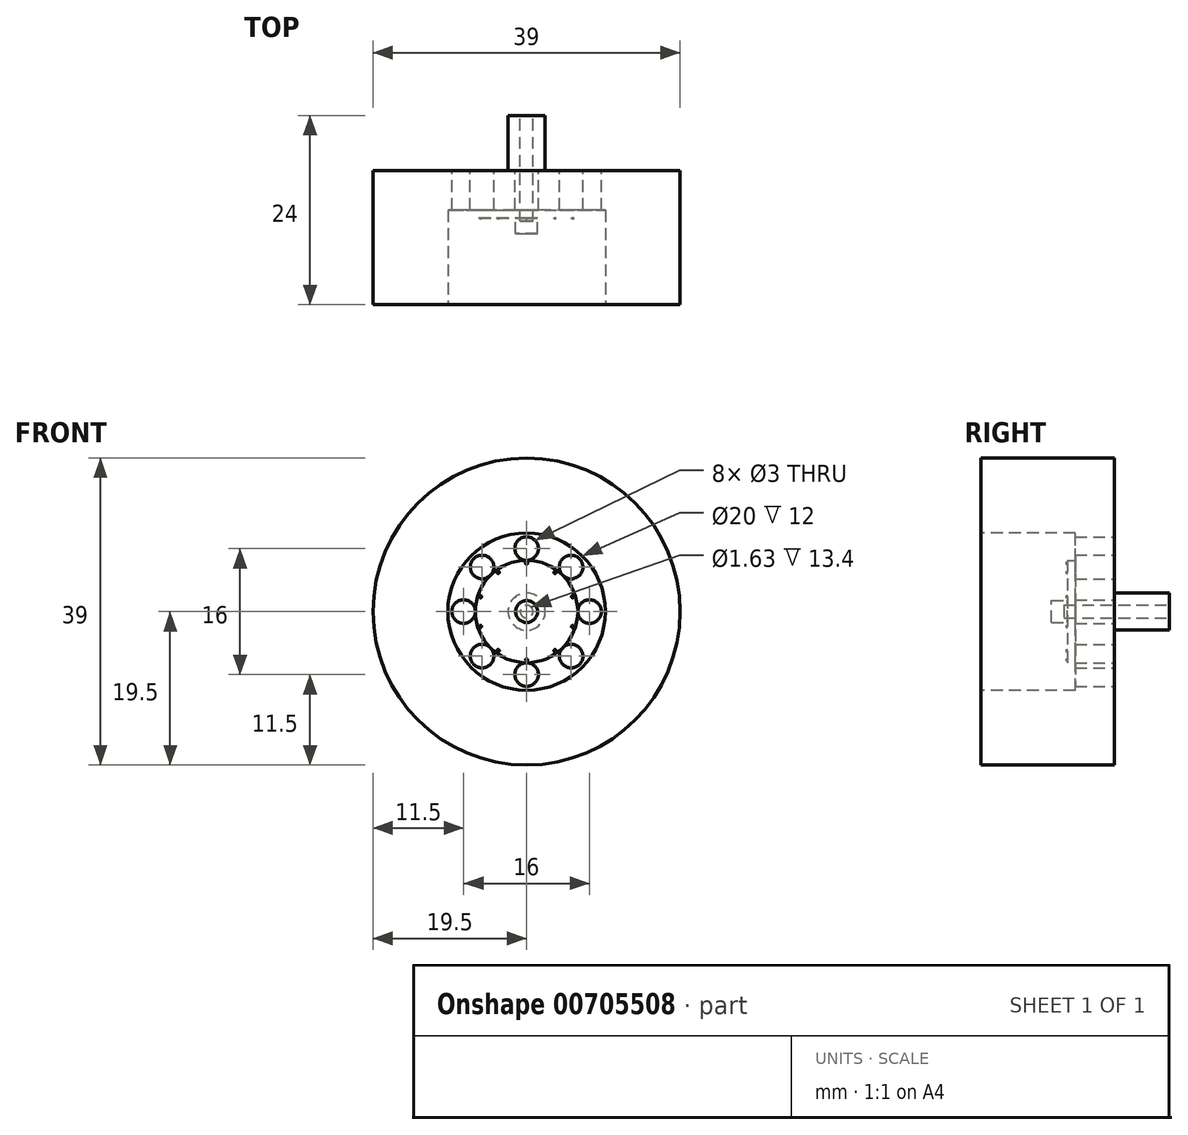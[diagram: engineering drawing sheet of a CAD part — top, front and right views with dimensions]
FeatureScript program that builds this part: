
annotation { "Feature Type Name" : "Feature", "Feature Type Description" : "" }
export const myFeature = defineFeature(function(context is Context, id is Id, definition is map)
    precondition{}
    {
        {
            var Q0;
            Q0=qCreatedBy(makeId("Front.planeOp"),FACE);
            var sketch = newSketch(context, id + "F0", { "sketchPlane" : qUnion([Q0])});
            skCircle(sketch, "E0", {"center": v(0, 0) * mm, "radius": 19.5 * mm});
            skSolve(sketch);
        }
        {
            var Q0;
            Q0 = qSketchRegion(id + "F0", true);
            extrude(context, id + "F1", {"entities" : qUnion([Q0]), "depth" : 17 * mm, "offsetDistance" : 25 * mm});
        }
        {
            var Q0;
            Q0=makeQuery(id+"F1.opExtrude","CAP_FACE",FACE,{"disambiguationData":[OSD([sQuery(id+"F0.wireOp",EDGE,"E0")])],"isStart":false});
            var sketch = newSketch(context, id + "F2", { "sketchPlane" : qUnion([Q0])});
            skCircle(sketch, "E1", {"center": v(0, 0) * mm, "radius": 10 * mm});
            skSolve(sketch);
        }
        {
            var Q0;
            Q0=makeQuery(id+"F2.imprint","IMPRINT",FACE,{"disambiguationData":[TD([[makeQuery(id+"F2.imprint","IMPRINT",EDGE,{"derivedFrom":sQuery(id+"F2.wireOp",EDGE,"E1")}),1.0]])]});
            extrude(context, id + "F3", {"entities" : qUnion([Q0]), "operationType" : NewBodyOperationType.REMOVE, "oppositeDirection" : true, "depth" : 12 * mm, "offsetDistance" : 25 * mm});
        }
        {
            var Q0;
            Q0=makeQuery(id+"F1.opExtrude","CAP_FACE",FACE,{"disambiguationData":[OSD([sQuery(id+"F0.wireOp",EDGE,"E0")])],"isStart":true});
            var sketch = newSketch(context, id + "F4", { "sketchPlane" : qUnion([Q0])});
            skCircle(sketch, "E2", {"center": v(0, 0) * mm, "radius": 6 * mm});
            skLineSegment(sketch, "E3", {"start": v(0, 6) * mm, "end": v(0, 7) * mm});
            skLineSegment(sketch, "E4", {"start": v(0, 7) * mm, "end": v(0, 8) * mm});
            skCircle(sketch, "E5", {"center": v(0, 8) * mm, "radius": 1.5 * mm});
            skCircle(sketch, "E6.1.0", {"center": v(-5.66, 5.66) * mm, "radius": 1.5 * mm});
            skCircle(sketch, "E6.2.0", {"center": v(-8, 0) * mm, "radius": 1.5 * mm});
            skCircle(sketch, "E6.3.0", {"center": v(-5.66, -5.66) * mm, "radius": 1.5 * mm});
            skCircle(sketch, "E6.4.0", {"center": v(0, -8) * mm, "radius": 1.5 * mm});
            skCircle(sketch, "E6.5.0", {"center": v(5.66, -5.66) * mm, "radius": 1.5 * mm});
            skCircle(sketch, "E6.6.0", {"center": v(8, 0) * mm, "radius": 1.5 * mm});
            skCircle(sketch, "E6.7.0", {"center": v(5.66, 5.66) * mm, "radius": 1.5 * mm});
            skLineSegment(sketch, "E7", {"start": v(0, 9.5) * mm, "end": v(0, 10.5) * mm});
            skCircle(sketch, "E8", {"center": v(0, 0) * mm, "radius": 10.5 * mm});
            skSolve(sketch);
        }
        {
            var Q0;
            Q0=makeQuery(id+"F4.imprint","IMPRINT",FACE,{"disambiguationData":[TD([[makeQuery(id+"F4.imprint","IMPRINT",EDGE,{"derivedFrom":sQuery(id+"F4.wireOp",EDGE,"E6.2.0")}),1.0]])]});
            var Q1;
            Q1=makeQuery(id+"F4.imprint","IMPRINT",FACE,{"disambiguationData":[TD([[makeQuery(id+"F4.imprint","IMPRINT",EDGE,{"derivedFrom":sQuery(id+"F4.wireOp",EDGE,"E6.1.0")}),1.0]])]});
            var Q2;
            {var subQ0=sQuery(id+"F4.wireOp",EDGE,"E5");var subQ1=makeQuery(id+"F4.imprint","IMPRINT",VERTEX,{"disambiguationData":[OD(0.0)],"derivedFrom":subQ0});Q2=makeQuery(id+"F4.imprint","IMPRINT",FACE,{"disambiguationData":[TD([[makeQuery(id+"F4.imprint","IMPRINT",EDGE,{"disambiguationData":[TD([[subQ1,-1.0]])],"derivedFrom":subQ0}),1.0]])]});}
            var Q3;
            Q3=makeQuery(id+"F4.imprint","IMPRINT",FACE,{"disambiguationData":[TD([[makeQuery(id+"F4.imprint","IMPRINT",EDGE,{"derivedFrom":sQuery(id+"F4.wireOp",EDGE,"E6.7.0")}),1.0]])]});
            var Q4;
            Q4=makeQuery(id+"F4.imprint","IMPRINT",FACE,{"disambiguationData":[TD([[makeQuery(id+"F4.imprint","IMPRINT",EDGE,{"derivedFrom":sQuery(id+"F4.wireOp",EDGE,"E6.6.0")}),1.0]])]});
            var Q5;
            Q5=makeQuery(id+"F4.imprint","IMPRINT",FACE,{"disambiguationData":[TD([[makeQuery(id+"F4.imprint","IMPRINT",EDGE,{"derivedFrom":sQuery(id+"F4.wireOp",EDGE,"E6.5.0")}),1.0]])]});
            var Q6;
            Q6=makeQuery(id+"F4.imprint","IMPRINT",FACE,{"disambiguationData":[TD([[makeQuery(id+"F4.imprint","IMPRINT",EDGE,{"derivedFrom":sQuery(id+"F4.wireOp",EDGE,"E6.4.0")}),1.0]])]});
            var Q7;
            Q7=makeQuery(id+"F4.imprint","IMPRINT",FACE,{"disambiguationData":[TD([[makeQuery(id+"F4.imprint","IMPRINT",EDGE,{"derivedFrom":sQuery(id+"F4.wireOp",EDGE,"E6.3.0")}),1.0]])]});
            extrude(context, id + "F5", {"entities" : qUnion([Q0, Q1, Q2, Q3, Q4, Q5, Q6, Q7]), "operationType" : NewBodyOperationType.REMOVE, "oppositeDirection" : true, "depth" : 25 * mm, "offsetDistance" : 25 * mm});
        }
        {
            var Q0;
            Q0=makeQuery(id+"F3.boolean.opBoolean","COPY",FACE,{"derivedFrom":makeQuery(id+"F3.opExtrude","CAP_FACE",FACE,{"disambiguationData":[OSD([sQuery(id+"F2.wireOp",EDGE,"E1")])],"isStart":false})});
            var sketch = newSketch(context, id + "F6", { "sketchPlane" : qUnion([Q0])});
            skCircle(sketch, "E9", {"center": v(0, 0) * mm, "radius": 6.5 * mm});
            skSolve(sketch);
        }
        {
            var Q0;
            Q0 = qSketchRegion(id + "F6", true);
            var Q1;
            {var subQ0=sQuery(id+"F6.wireOp",EDGE,"E9");var subQ1=makeQuery(id+"F3.boolean.opBoolean","COPY",FACE,{"derivedFrom":makeQuery(id+"F3.opExtrude","CAP_FACE",FACE,{"disambiguationData":[OSD([sQuery(id+"F2.wireOp",EDGE,"E1")])],"isStart":false})});var subQ5=makeQuery(id+"F6.imprint","INTERSECT",VERTEX,{"derivedFrom":[makeQuery(id+"F5.boolean.opBoolean","INTERSECT",EDGE,{"derivedFrom":[subQ1,makeQuery(id+"F5.opExtrude","SWEPT_FACE",FACE,{"disambiguationData":[OSD([sQuery(id+"F4.wireOp",EDGE,"E6.1.0")])]})]}),subQ0]});Q1=makeQuery(id+"F6.imprint","IMPRINT",FACE,{"disambiguationData":[TD([[makeQuery(id+"F6.imprint","IMPRINT",EDGE,{"disambiguationData":[TD([[subQ5,1.0]])],"derivedFrom":subQ0}),1.0]])]});}
            extrude(context, id + "F7", {"entities" : qUnion([Q0, Q1]), "operationType" : NewBodyOperationType.ADD, "depth" : 1 * mm, "offsetDistance" : 25 * mm});
        }
        {
            var Q0;
            Q0=makeQuery(id+"F7.opExtrude","CAP_FACE",FACE,{"disambiguationData":[OSD([sQuery(id+"F6.wireOp",EDGE,"E9")])],"isStart":false});
            var sketch = newSketch(context, id + "F8", { "sketchPlane" : qUnion([Q0])});
            skCircle(sketch, "E10", {"center": v(0, 6.15) * mm, "radius": 0.15 * mm});
            skCircle(sketch, "E11.1.0", {"center": v(-3.61, 4.97) * mm, "radius": 0.15 * mm});
            skCircle(sketch, "E11.2.0", {"center": v(-5.84, 1.9) * mm, "radius": 0.15 * mm});
            skCircle(sketch, "E11.3.0", {"center": v(-5.84, -1.9) * mm, "radius": 0.15 * mm});
            skCircle(sketch, "E11.4.0", {"center": v(-3.61, -4.97) * mm, "radius": 0.15 * mm});
            skCircle(sketch, "E11.5.0", {"center": v(0, -6.15) * mm, "radius": 0.15 * mm});
            skCircle(sketch, "E11.6.0", {"center": v(3.61, -4.97) * mm, "radius": 0.15 * mm});
            skCircle(sketch, "E11.7.0", {"center": v(5.84, -1.9) * mm, "radius": 0.15 * mm});
            skCircle(sketch, "E11.8.0", {"center": v(5.84, 1.9) * mm, "radius": 0.15 * mm});
            skCircle(sketch, "E11.9.0", {"center": v(3.61, 4.97) * mm, "radius": 0.15 * mm});
            skPoint(sketch, "E11.center", {"position": v(0, 0) * mm});
            skSolve(sketch);
        }
        {
            var Q0;
            Q0 = qSketchRegion(id + "F8", true);
            extrude(context, id + "F9", {"entities" : qUnion([Q0]), "operationType" : NewBodyOperationType.ADD, "depth" : .1 * mm, "offsetDistance" : 25 * mm});
        }
        {
            var Q0;
            Q0=makeQuery(id+"F7.opExtrude","CAP_FACE",FACE,{"disambiguationData":[OSD([sQuery(id+"F6.wireOp",EDGE,"E9")])],"isStart":false});
            var sketch = newSketch(context, id + "F10", { "sketchPlane" : qUnion([Q0])});
            skSolve(sketch);
        }
        {
            var Q0;
            Q0=makeQuery(id+"F10.imprint","IMPRINT",FACE,{"disambiguationData":[TD([[makeQuery(id+"F10.imprint","IMPRINT",EDGE,{"derivedFrom":makeQuery(id+"F7.opExtrude","CAP_EDGE",EDGE,{"disambiguationData":[OSD([sQuery(id+"F6.wireOp",EDGE,"E9")])],"isStart":false})}),1.0]])]});
            var sketch = newSketch(context, id + "F11", { "sketchPlane" : qUnion([Q0])});
            skCircle(sketch, "E12", {"center": v(0, 0) * mm, "radius": 1.39 * mm});
            skSolve(sketch);
        }
        {
            var Q0;
            Q0=makeQuery(id+"F11.imprint","IMPRINT",FACE,{"disambiguationData":[TD([[makeQuery(id+"F11.imprint","IMPRINT",EDGE,{"derivedFrom":sQuery(id+"F11.wireOp",EDGE,"E12")}),1.0]])]});
            extrude(context, id + "F12", {"entities" : qUnion([Q0]), "operationType" : NewBodyOperationType.ADD, "depth" : 2 * mm, "offsetDistance" : 25 * mm});
        }
        {
            var Q0;
            Q0=makeQuery(id+"F1.opExtrude","CAP_FACE",FACE,{"disambiguationData":[OSD([sQuery(id+"F0.wireOp",EDGE,"E0")])],"isStart":true});
            var sketch = newSketch(context, id + "F13", { "sketchPlane" : qUnion([Q0])});
            skCircle(sketch, "E13", {"center": v(0, 0) * mm, "radius": 2.36 * mm});
            skSolve(sketch);
        }
        {
            var Q0;
            Q0=makeQuery(id+"F13.imprint","IMPRINT",FACE,{"disambiguationData":[TD([[makeQuery(id+"F13.imprint","IMPRINT",EDGE,{"derivedFrom":sQuery(id+"F13.wireOp",EDGE,"E13")}),1.0]])]});
            extrude(context, id + "F14", {"entities" : qUnion([Q0]), "operationType" : NewBodyOperationType.ADD, "depth" : 7 * mm, "offsetDistance" : 25 * mm});
        }
        {
            var Q0;
            Q0=makeQuery(id+"F14.opExtrude","CAP_FACE",FACE,{"disambiguationData":[OSD([sQuery(id+"F13.wireOp",EDGE,"E13")])],"isStart":false});
            var sketch = newSketch(context, id + "F15", { "sketchPlane" : qUnion([Q0])});
            skCircle(sketch, "E14", {"center": v(0, 0) * mm, "radius": 0.81 * mm});
            skSolve(sketch);
        }
        {
            var Q0;
            Q0=makeQuery(id+"F15.imprint","IMPRINT",FACE,{"disambiguationData":[TD([[makeQuery(id+"F15.imprint","IMPRINT",EDGE,{"derivedFrom":sQuery(id+"F15.wireOp",EDGE,"E14")}),1.0]])]});
            extrude(context, id + "F16", {"entities" : qUnion([Q0]), "operationType" : NewBodyOperationType.REMOVE, "oppositeDirection" : true, "depth" : 13.4 * mm, "offsetDistance" : 25 * mm});
        }
    });
